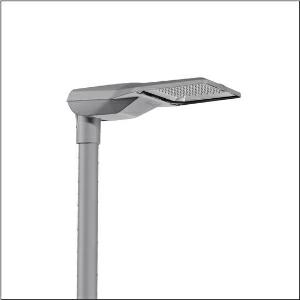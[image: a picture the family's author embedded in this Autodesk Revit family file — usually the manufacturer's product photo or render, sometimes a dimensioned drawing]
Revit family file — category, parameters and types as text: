
# Revit family: streetlight_sl_21_midi___stw1_0a_5xe7e23a08nb_e8ed
name_source: partatom
category: Lighting Fixtures
units: mm (PartAtom-declared; Revit-internal decimal feet)

## family parameters
Cut with Voids When Loaded = No
Host = Face
Light Source = No
Part Type = Normal
Room Calculation Point = No
Round Connector Dimension = Use Diameter
Shared = No

## types (1)
- --- (1 x LED, 18780 lm, 151.2 W, 2200K)
    Apparent Load = 151 VA
    CIE Flux Codes = 39 75 98 100 100
    Color Rendering = 70
    Color Temperature = 2200K
    Default Elevation = 1800 mm
    Description = Streetlight SL 21 midi, mast luminaire, primary light control with lens, of PMMA, primary optical cover: cover, of toughened safety glass, transparent, light distribution: STW1.0a, light emission: direct distribution, primary light characteristic: asymmetric, installation type: post-top, side-entry, LED, 3G 1.5mm², High Power LED, rated luminous flux: 18.780lm, luminous efficacy: 124lm/W, light colour: 722, colour temperature: 2200K, control: overheat protection, constant luminous flux control, time-dependent luminous flux control, flexible luminous flux parameterisation, mains connection: 220..240V, AC, 50/60Hz, connection cable pre-assembled, cable length: 12,5m, wiring characteristics: H07RN-F, start of lifetime: 151W, end of service life: 157W, reduction: 70W, luminaire housing, of diecast aluminium, powder-coated, Siteco® metallic grey (DB 702S), corrosivity category C5 mid according to DIN EN ISO 12944, please order mast flange separately, inclination adjustable: 0°, 5°, 10°, 15°, sealing non-destructively replaceable, multi-level sealing system, length: 644mm, width: 335mm, height: 110mm, mast flange for spigot size: 42mm (side-entry): 5XC10008XM4, 60/48mm (side-entry/post-top): 5XC10108XM2, 76/60mm (side-entry/post-top): 5XC10108XM1, protection rating (complete): IP66, insulation class (complete): insulation class II (safety insulation), certification: CE, ENEC, ENEC+, VDE, impact resistance: IK09, permissible operating ambient temperature for outdoor applications: -40..+50°C, standard-compliant lighting for roads and squares, packaging unit: 1 piece

Light Distribution: STW1.0a
    Height = 111 mm
    Lamp = 1 x LED
    Lamp Light Flux = 18780 lm
    Lamp Power = 151.2 W
    Lamp count = 1
    Length = 644 mm
    Luminous efficacy = 124 lm/W
    Manufacturer = Siteco
    ModVariant = No
    Model = 5XE7E23A08NB
    Number of Poles = 1
    OnlyDefault = Yes
    Power Factor = 1
    Product Name = Streetlight SL 21 midi | STW1.0a
    Product group = mast luminaire | pylon top
    ProductGroupID = 6100
    Protection Class = Protection class II
    Protection Degree = IP 66
    RLX_Detail_Level = 1
    RLX_Emergency_Light_Flux = 0 lm
    RLX_Emergency_Type = 0
    RLX_Emergency_Type_DB = No
    RlxData = <blob elided: 90705 chars, md5=b08e9377>
    Socket = socket
    Standby Power = 0 W
    System Light Flux = 18781 lm
    System Power = 151 W
    Type Comments = factory setting: luminous flux: 100 % | Output Level: 100 % | 802 mA
    Type Image = l_1004298.jpg
    URL = http://relux.com
    VarID = @adj_119891
    Voltage = 0 V
    Weight = 0.00 kg
    Width = 336 mm

## geometry (parser evidence)
native form markers: Blend x4, Sweep x11
no freeform markers — native parametric forms only
